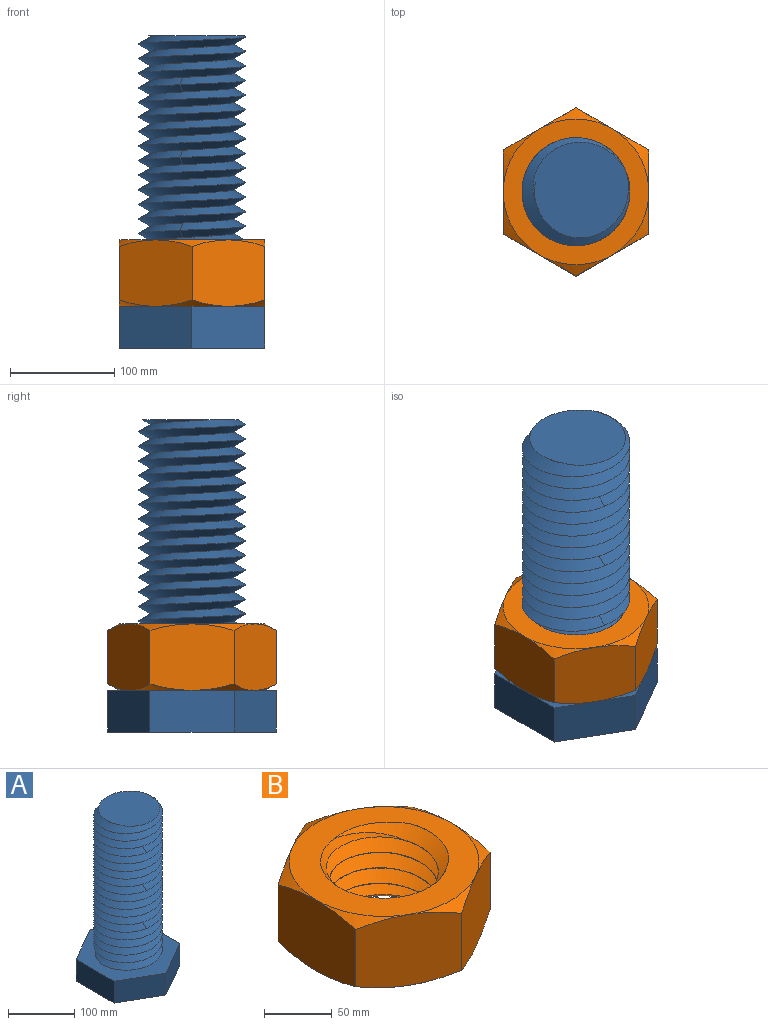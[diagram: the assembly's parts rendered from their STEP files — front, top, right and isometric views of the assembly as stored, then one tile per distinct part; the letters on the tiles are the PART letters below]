
ASSEMBLY  parts=2 mates=1
PART A: 18 faces, bbox 149.9x171.5x318.3 mm
  f0: cylinder r=40mm len=260mm, axis (0,0,-1), area 1678.9mm2, adj f1,f2,f3,f4,f5,f6,f7,f8
  f1: plane 101.83x101.76mm, normal (0,0,1), area 6630.3mm2, adj f0,f2,f3
  f2: bspline ~119.78x103.73mm, area 14186.3mm2, adj f0,f1,f3,f8
  f3: bspline ~119.78x103.73mm, area 12335.4mm2, adj f0,f1,f2,f9
  f4: bspline ~119.78x103.73mm, area 21597.9mm2, adj f0,f5,f7,f10
  f5: bspline ~119.78x103.73mm, area 19768.3mm2, adj f0,f4,f6,f10
  f6: bspline ~119.78x103.73mm, area 19786.9mm2, adj f0,f5,f7,f8
  f7: bspline ~119.78x103.73mm, area 19782.7mm2, adj f0,f4,f6,f9
  f8: bspline ~119.78x103.73mm, area 19786.9mm2, adj f0,f2,f6,f9
  f9: bspline ~119.78x103.73mm, area 19782.7mm2, adj f0,f3,f7,f8
  f10: plane 171.1x149.44mm, normal (0,0,1), area 10344.3mm2, adj f0,f4,f5,f11,f12,f13,f14,f15
  f11: plane 80.83x40mm, normal (1,0,0), area 3233.2mm2, adj f10,f12,f16,f17
  f12: plane 70x40.41mm, normal (0.5,0.87,0), area 3233.2mm2, adj f10,f11,f13,f17
  f13: plane 70x40.41mm, normal (-0.5,0.87,0), area 3233.2mm2, adj f10,f12,f14,f17
  f14: plane 80.83x40mm, normal (-1,0,0), area 3233.2mm2, adj f10,f13,f15,f17
  f15: plane 70x40.41mm, normal (-0.5,-0.87,0), area 3233.2mm2, adj f10,f14,f16,f17
  f16: plane 70x40.41mm, normal (0.5,-0.87,0), area 3233.2mm2, adj f10,f11,f15,f17
  f17: plane 161.66x140mm, normal (0,0,-1), area 16974.1mm2, adj f11,f12,f13,f14,f15,f16
PART B: 25 faces, bbox 164.1x164.1x83.8 mm
  f0: plane 70.01x64.02mm, normal (0.5,-0.87,0), area 4826.4mm2, adj f1,f5,f13,f14,f15,f16
  f1: plane 80.86x64.02mm, normal (1,0,0), area 4826.4mm2, adj f0,f2,f9,f14,f15,f20
  f2: plane 70.01x64.02mm, normal (0.5,0.87,0), area 4826.4mm2, adj f1,f3,f9,f10,f19,f20
  f3: plane 70.01x64.02mm, normal (-0.5,0.87,0), area 4826.4mm2, adj f2,f4,f10,f11,f18,f19
  f4: plane 80.86x64.02mm, normal (-1,0,0), area 4826.4mm2, adj f3,f5,f11,f12,f17,f18
  f5: plane 70.01x64.02mm, normal (-0.5,-0.87,0), area 4826.4mm2, adj f0,f4,f12,f13,f16,f17
  f6: plane 142.45x142.45mm, normal (0,0,-1), area 8196.9mm2, adj f15,f16,f17,f18,f19,f20,f22,f23
  f7: plane 141.99x141.99mm, normal (0,0,1), area 8198.1mm2, adj f9,f10,f11,f12,f13,f14,f21,f23
  f8: cylinder r=40mm len=80mm, axis (0,0,-1), area 395.6mm2, adj f21,f22,f23,f24
  f9: cone r=70mm half-angle=60deg, axis (0,0,-1), area 304.1mm2, adj f1,f2,f7
  f10: cone r=70mm half-angle=60deg, axis (0,0,-1), area 304.1mm2, adj f2,f3,f7
  f11: cone r=70mm half-angle=60deg, axis (0,0,-1), area 304.1mm2, adj f3,f4,f7
  f12: cone r=70mm half-angle=60deg, axis (0,0,-1), area 304.1mm2, adj f4,f5,f7
  f13: cone r=70mm half-angle=60deg, axis (0,0,-1), area 304.1mm2, adj f0,f5,f7
  f14: cone r=70mm half-angle=60deg, axis (0,0,-1), area 304.1mm2, adj f0,f1,f7
  f15: cone r=70mm half-angle=60deg, axis (0,0,1), area 304.1mm2, adj f0,f1,f6
  f16: cone r=70mm half-angle=60deg, axis (0,0,1), area 304.1mm2, adj f0,f5,f6
  f17: cone r=70mm half-angle=60deg, axis (0,0,1), area 304.1mm2, adj f4,f5,f6
  f18: cone r=70mm half-angle=60deg, axis (0,0,1), area 304.1mm2, adj f3,f4,f6
  f19: cone r=70mm half-angle=60deg, axis (0,0,1), area 304.1mm2, adj f2,f3,f6
  f20: cone r=70mm half-angle=60deg, axis (0,0,1), area 304.1mm2, adj f1,f2,f6
  f21: cone r=40mm half-angle=45deg, axis (0,0,1), area 801mm2, adj f7,f8,f23,f24
  f22: cone r=46.76mm half-angle=45deg, axis (0,0,-1), area 798mm2, adj f6,f8,f23,f24
  f23: bspline ~119.78x103.73mm, area 17104.7mm2, adj f6,f7,f8,f21,f22,f24
  f24: bspline ~119.78x103.73mm, area 17106.2mm2, adj f6,f7,f8,f21,f22,f23
PLACE A at identity fixed
PLACE B at identity
MATE cylindrical A.f0 <-> B.f8  axis (0,0,1) through (0,0,-30.4)mm
